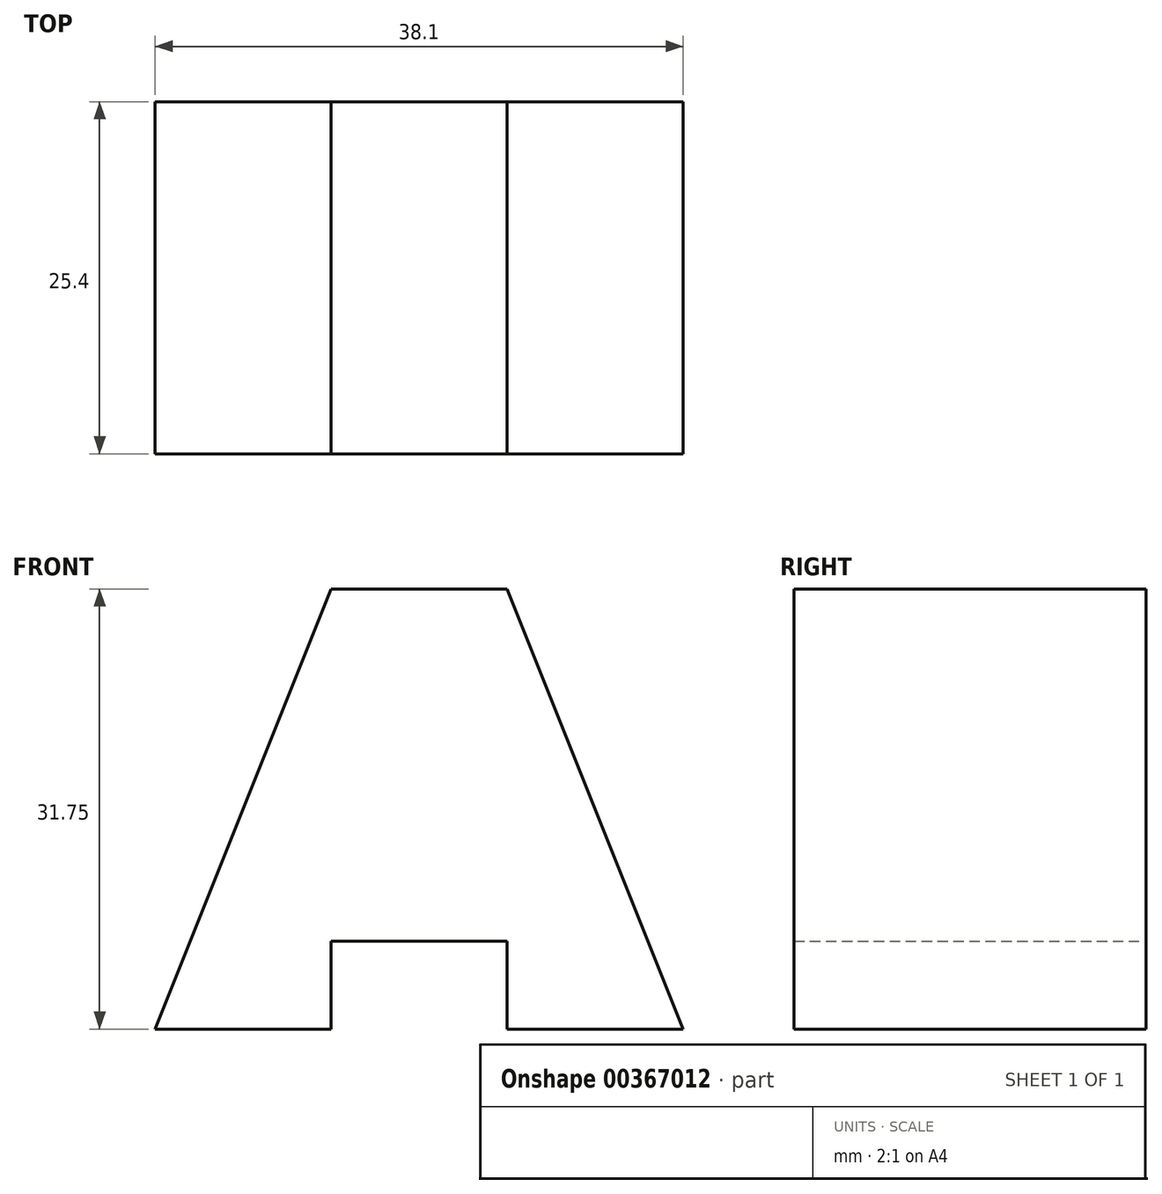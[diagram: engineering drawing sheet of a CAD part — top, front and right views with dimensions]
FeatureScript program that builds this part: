
annotation { "Feature Type Name" : "Feature", "Feature Type Description" : "" }
export const myFeature = defineFeature(function(context is Context, id is Id, definition is map)
    precondition{}
    {
        {
            var Q0;
            Q0=qCreatedBy(makeId("Front.planeOp"),FACE);
            var sketch = newSketch(context, id + "F0", { "sketchPlane" : qUnion([Q0])});
            skLineSegment(sketch, "E0", {"start": v(0, 0) * mm, "end": v(0, 31.75) * mm});
            skLineSegment(sketch, "E1", {"start": v(0, 31.75) * mm, "end": v(38.1, 31.75) * mm});
            skLineSegment(sketch, "E2", {"start": v(38.1, 31.75) * mm, "end": v(38.1, 0) * mm});
            skLineSegment(sketch, "E3", {"start": v(38.1, 0) * mm, "end": v(25.4, 0) * mm});
            skLineSegment(sketch, "E4", {"start": v(25.4, 0) * mm, "end": v(25.4, 6.35) * mm});
            skLineSegment(sketch, "E5", {"start": v(25.4, 6.35) * mm, "end": v(12.7, 6.35) * mm});
            skLineSegment(sketch, "E6", {"start": v(12.7, 6.35) * mm, "end": v(12.7, 0) * mm});
            skLineSegment(sketch, "E7", {"start": v(12.7, 0) * mm, "end": v(0, 0) * mm});
            skSolve(sketch);
        }
        {
            var Q0;
            Q0 = qSketchRegion(id + "F0", true);
            extrude(context, id + "F1", {"entities" : qUnion([Q0]), "depth" : 25.4 * mm});
        }
        {
            var Q0;
            Q0=makeQuery(id+"F1.opExtrude","CAP_FACE",FACE,{"disambiguationData":[OSD([sQuery(id+"F0.wireOp",EDGE,"E0"),sQuery(id+"F0.wireOp",EDGE,"E1"),sQuery(id+"F0.wireOp",EDGE,"E2"),sQuery(id+"F0.wireOp",EDGE,"E3"),sQuery(id+"F0.wireOp",EDGE,"E4"),sQuery(id+"F0.wireOp",EDGE,"E5"),sQuery(id+"F0.wireOp",EDGE,"E6"),sQuery(id+"F0.wireOp",EDGE,"E7")])],"isStart":false});
            var sketch = newSketch(context, id + "F2", { "sketchPlane" : qUnion([Q0])});
            skLineSegment(sketch, "E8", {"start": v(0, 0) * mm, "end": v(12.7, 31.75) * mm});
            skLineSegment(sketch, "E9", {"start": v(12.7, 31.75) * mm, "end": v(25.38, 31.75) * mm});
            skLineSegment(sketch, "E10", {"start": v(25.38, 31.75) * mm, "end": v(38.1, 0) * mm});
            skLineSegment(sketch, "E11", {"start": v(0, 0) * mm, "end": v(0, 31.75) * mm});
            skLineSegment(sketch, "E12", {"start": v(0, 31.75) * mm, "end": v(12.7, 31.75) * mm});
            skLineSegment(sketch, "E13", {"start": v(25.38, 31.75) * mm, "end": v(38.1, 31.75) * mm});
            skLineSegment(sketch, "E14", {"start": v(38.1, 31.75) * mm, "end": v(38.1, 0) * mm});
            skSolve(sketch);
        }
        {
            var Q0;
            Q0 = qSketchRegion(id + "F2", true);
            extrude(context, id + "F3", {"entities" : qUnion([Q0]), "operationType" : NewBodyOperationType.REMOVE, "oppositeDirection" : true, "depth" : 25.4 * mm});
        }
    });
